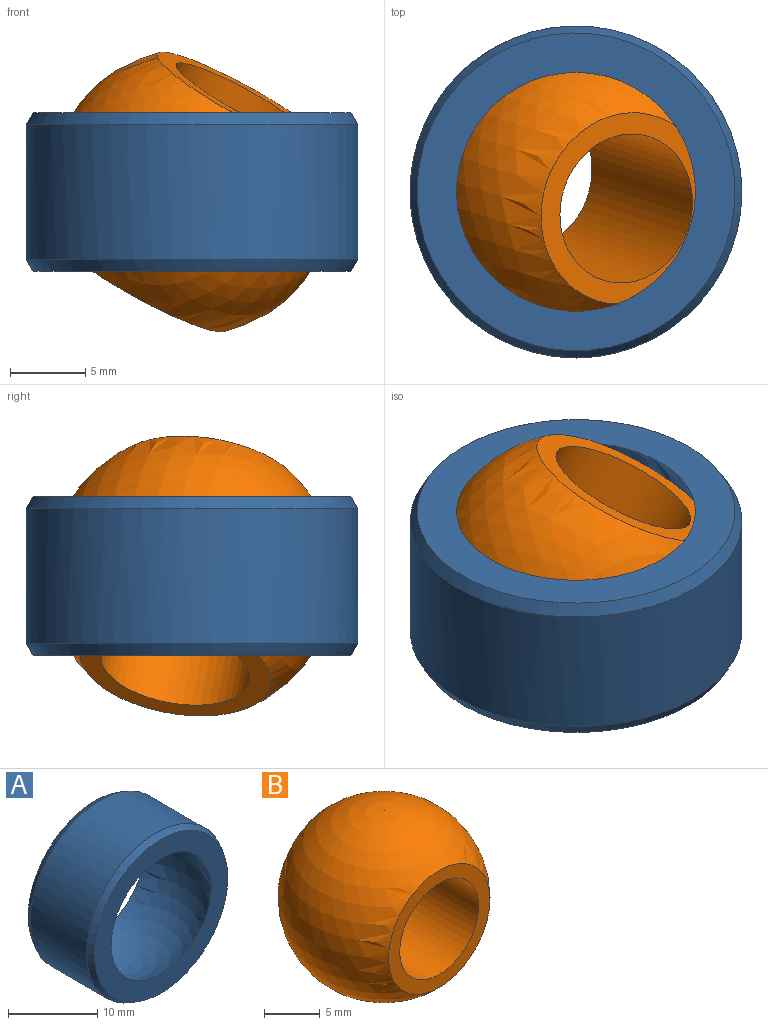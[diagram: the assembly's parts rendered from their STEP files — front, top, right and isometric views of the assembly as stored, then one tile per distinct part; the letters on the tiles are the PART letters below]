
ASSEMBLY  parts=2 mates=1
PART A: 6 faces, bbox 22x19x22 mm
  f0: cylinder r=11mm len=22mm, axis (0,-1,0), area 615.1mm2, adj f2,f3
  f1: sphere r=9.5mm, area 626.7mm2, adj f4,f5
  f2: cone r=10.77mm half-angle=30deg, axis (0,-1,0), area 62.5mm2, adj f0,f4
  f3: cone r=10.77mm half-angle=30deg, axis (0,1,0), area 62.5mm2, adj f0,f5
  f4: plane 21.08x21.08mm, normal (0,1,0), area 151.9mm2, adj f1,f2
  f5: plane 21.08x21.08mm, normal (0,-1,0), area 151.9mm2, adj f1,f3
PART B: 4 faces, bbox 19x19x19 mm
  f0: sphere r=9.5mm, area 835.7mm2, adj f2,f3
  f1: cylinder r=5mm len=14mm, axis (0,1,0), area 439.8mm2, adj f2,f3
  f2: plane 12.85x12.85mm, normal (0,-1,0), area 51.1mm2, adj f0,f1
  f3: plane 12.85x12.85mm, normal (0,1,0), area 51.1mm2, adj f0,f1
PLACE A rot(axis=(1,0,0),90deg) t=(0,0,5.25)mm
PLACE B rot(axis=(-0.91,0.4,0.11),90deg) t=(0,0,5.25)mm
MATE ball B.f1 <-> A.f0  axis (-0.48,0.16,-0.87) through (0,0,5.25)mm
